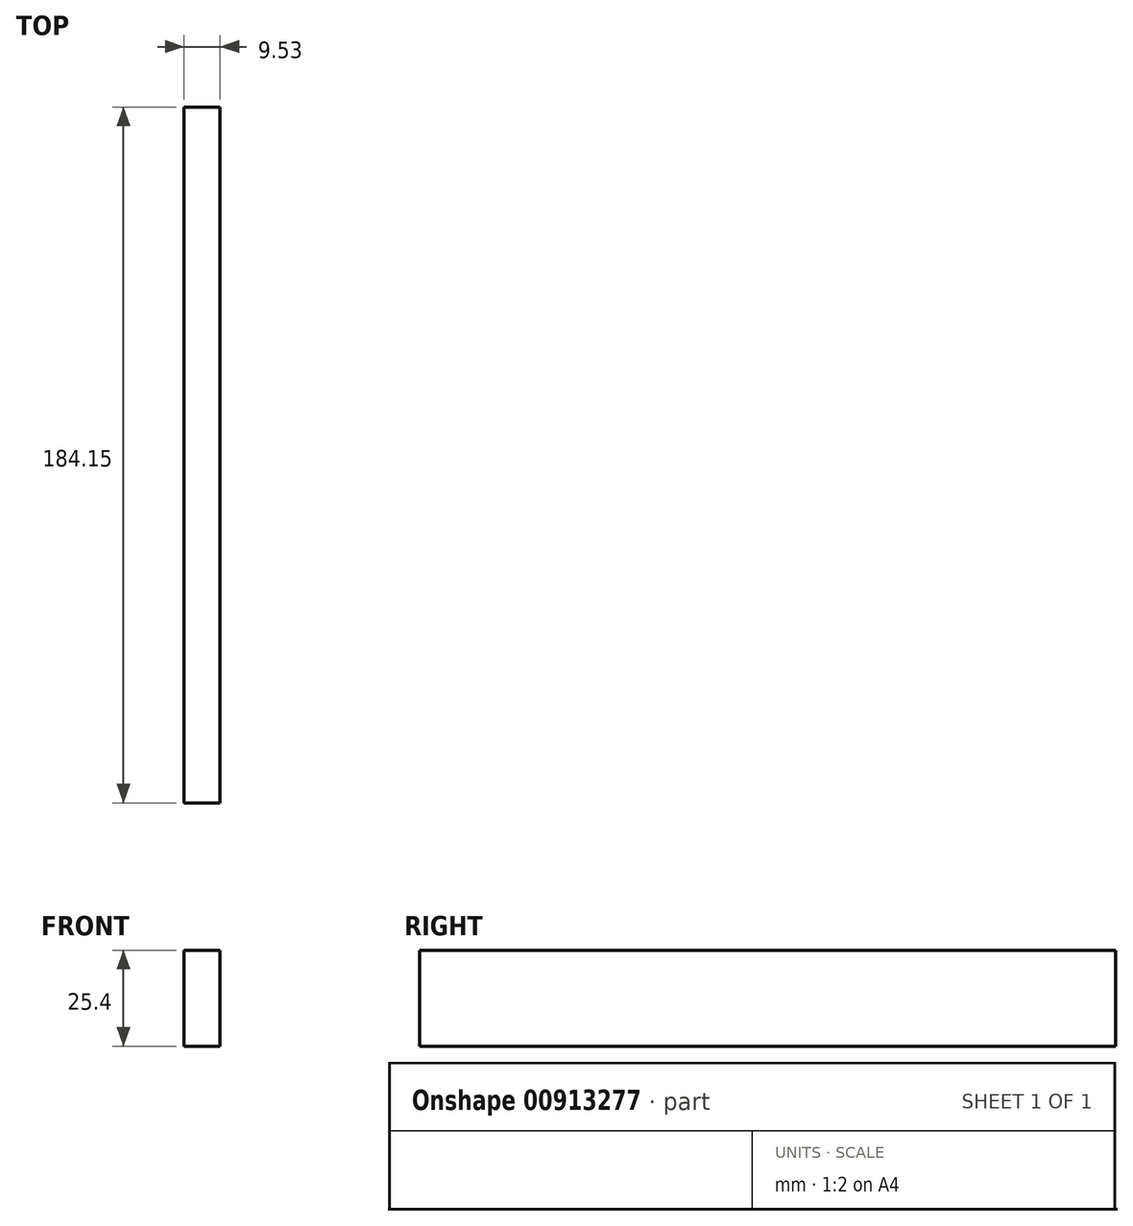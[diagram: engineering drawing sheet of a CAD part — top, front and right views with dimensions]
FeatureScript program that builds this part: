
annotation { "Feature Type Name" : "Feature", "Feature Type Description" : "" }
export const myFeature = defineFeature(function(context is Context, id is Id, definition is map)
    precondition{}
    {
        {
            var Q0;
            Q0=qCreatedBy(makeId("Top.planeOp"),FACE);
            var sketch = newSketch(context, id + "F0", { "sketchPlane" : qUnion([Q0])});
            skLineSegment(sketch, "E0.bottom", {"start": v(-146.73, 92.8) * mm, "end": v(-156.26, 92.8) * mm});
            skLineSegment(sketch, "E0.top", {"start": v(-146.73, -91.35) * mm, "end": v(-156.26, -91.35) * mm});
            skLineSegment(sketch, "E0.left", {"start": v(-146.73, 92.8) * mm, "end": v(-146.73, -91.35) * mm});
            skLineSegment(sketch, "E0.right", {"start": v(-156.26, 92.8) * mm, "end": v(-156.26, -91.35) * mm});
            skSolve(sketch);
        }
        {
            var Q0;
            Q0=makeQuery(id+"F0.imprint","IMPRINT",FACE,{"disambiguationData":[TD([[makeQuery(id+"F0.imprint","IMPRINT",EDGE,{"derivedFrom":sQuery(id+"F0.wireOp",EDGE,"E0.bottom")}),1.0]])]});
            extrude(context, id + "F1", {"entities" : qUnion([Q0]), "depth" : 25.4 * mm, "offsetDistance" : 25.4 * mm});
        }
    });
